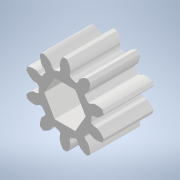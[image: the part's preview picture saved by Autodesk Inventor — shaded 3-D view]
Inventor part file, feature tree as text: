
AUTODESK INVENTOR PART (.ipt)
format: ipt  version: 2022 (Build 260153000, 153)  size: 901,120 bytes
history: native  units: mm
features: extrude x2, sketch x2
ambient origin geometry x8: Origin, YZ Plane, XZ Plane, XY Plane, X Axis, Y Axis, Z Axis, Center Point
bodies: Solid1 (feature_tree)
feature tree (4):
  extrude  "Extrusion1"  Depth=7.8mm
  extrude  "Extrusion2"  Depth=8.0mm TaperAngle=0.0deg
  sketch  "Sketch1"  dims[d0=7.8mm d1=0.0mm d2=3.1mm]
  sketch  "Sketch2"  dims[d3=60.0mm d5=360.0deg d7=8.0mm d8=0.0mm d9=0.45mm]
